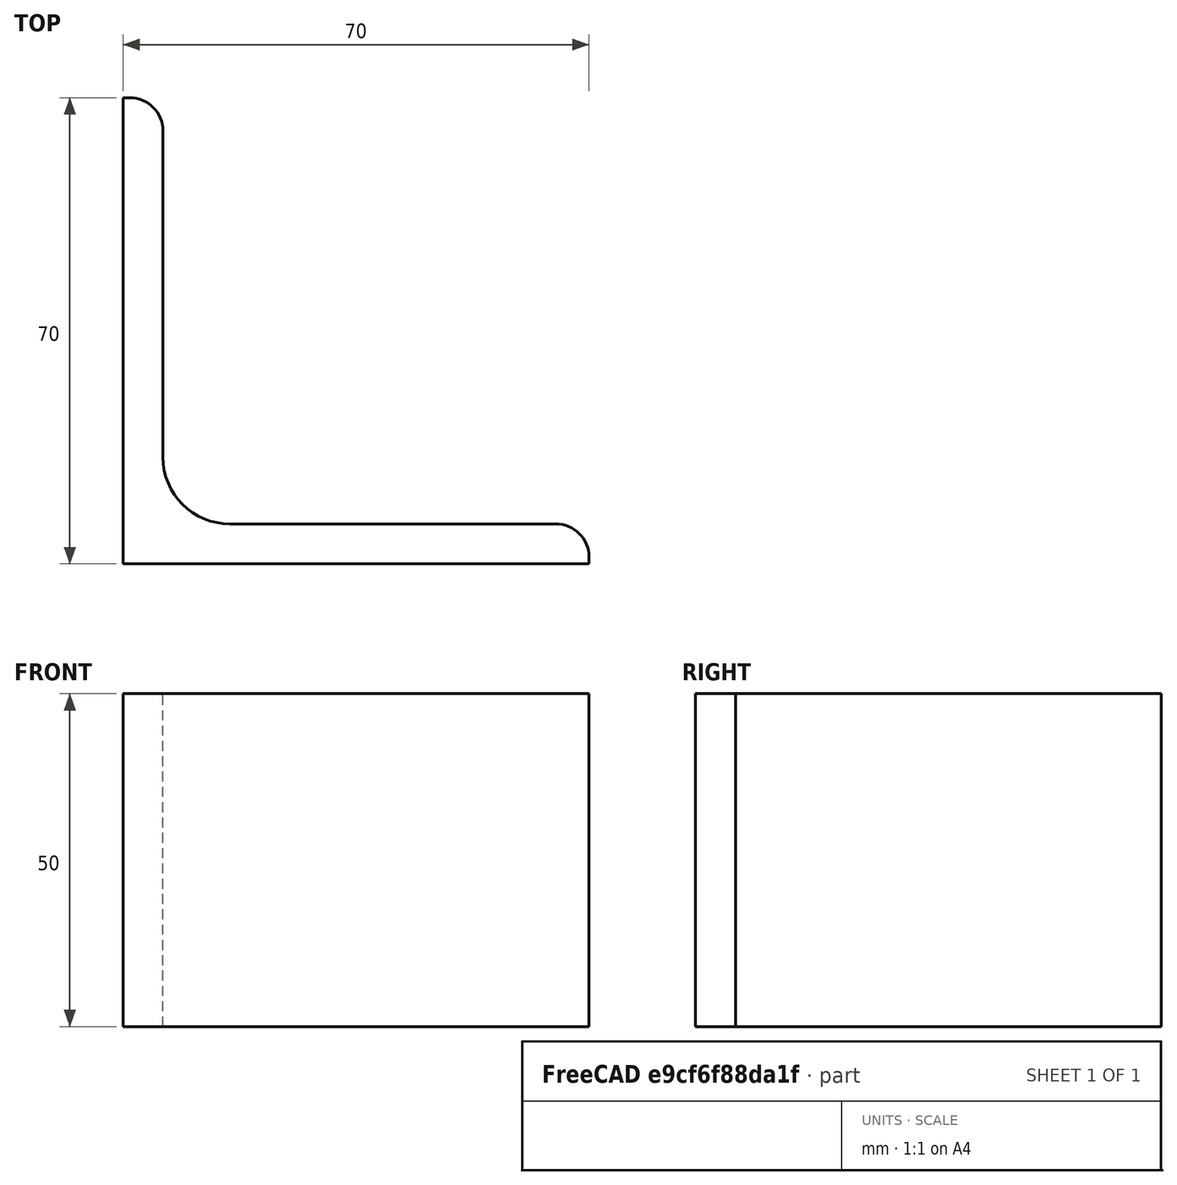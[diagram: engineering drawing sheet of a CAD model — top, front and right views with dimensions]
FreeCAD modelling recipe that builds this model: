
FCSTD DOCUMENT  (FreeCAD 0.15R4671 (Git))
Label: Angle Bar L70x70x6 EN10056 S235JR
License: All rights reserved
LicenseURL: http://en.wikipedia.org/wiki/All_rights_reserved
objects: Sketcher::SketchObject×1, Part::Extrusion×1
note: 2 computed .brp shape members not serialized (recipe doc carries the construction recipe); baked Part::Feature solids carry a one-line shape summary decoded from their .brp

FEATURE [Sketcher::SketchObject] Sketch
  sketch-geometry (9):
    g0: LineSegment StartX=0 StartY=0 StartZ=0 EndX=70 EndY=0 EndZ=0
    g1: LineSegment StartX=70 StartY=0 StartZ=0 EndX=70 EndY=1 EndZ=0
    g2: LineSegment StartX=65 StartY=6 StartZ=0 EndX=16 EndY=6 EndZ=0
    g3: LineSegment StartX=0 StartY=0 StartZ=0 EndX=0 EndY=70 EndZ=0
    g4: LineSegment StartX=0 StartY=70 StartZ=0 EndX=1 EndY=70 EndZ=0
    g5: LineSegment StartX=6 StartY=65 StartZ=0 EndX=6 EndY=16 EndZ=0
    g6: ArcOfCircle CenterX=16 CenterY=16 CenterZ=0 NormalX=0 NormalY=0 NormalZ=1 Radius=10 StartAngle=3.14159 EndAngle=4.71239
    g7: ArcOfCircle CenterX=1 CenterY=65 CenterZ=0 NormalX=0 NormalY=0 NormalZ=1 Radius=5 StartAngle=0 EndAngle=1.5708
    g8: ArcOfCircle CenterX=65 CenterY=1 CenterZ=0 NormalX=0 NormalY=0 NormalZ=1 Radius=5 StartAngle=0 EndAngle=1.5708
  constraints (23):
    c: Coincident(g0,g-1)
    c: Horizontal(g0)
    c: Coincident(g1,g0)
    c: Vertical(g1)
    c: Horizontal(g2)
    c: Coincident(g3,g-1)
    c: Vertical(g3)
    c: Coincident(g4,g3)
    c: Horizontal(g4)
    c: Vertical(g5)
    c: Tangent(g5,g6) = -1.5708
    c: Tangent(g2,g6) = 1.5708
    c: Tangent(g4,g7) = 1.5708
    c: Tangent(g5,g7) = 1.5708
    c: Tangent(g2,g8) = -1.5708
    c: Tangent(g1,g8) = -1.5708
    c: DistanceX(g0) = 70
    c: DistanceY(g3) = 70
    c: DistanceY(g0,g2) = 6
    c: DistanceX(g3,g5) = 6
    c: Radius(g6) = 10
    c: Radius(g8) = 5
    c: Radius(g7) = 5
FEATURE [Part::Extrusion] Extrude  label="Angle Bar L70x70x6 EN10056 S235JR"
  Base = -> Sketch
  Dir = (0,0,50)
  Solid = true
